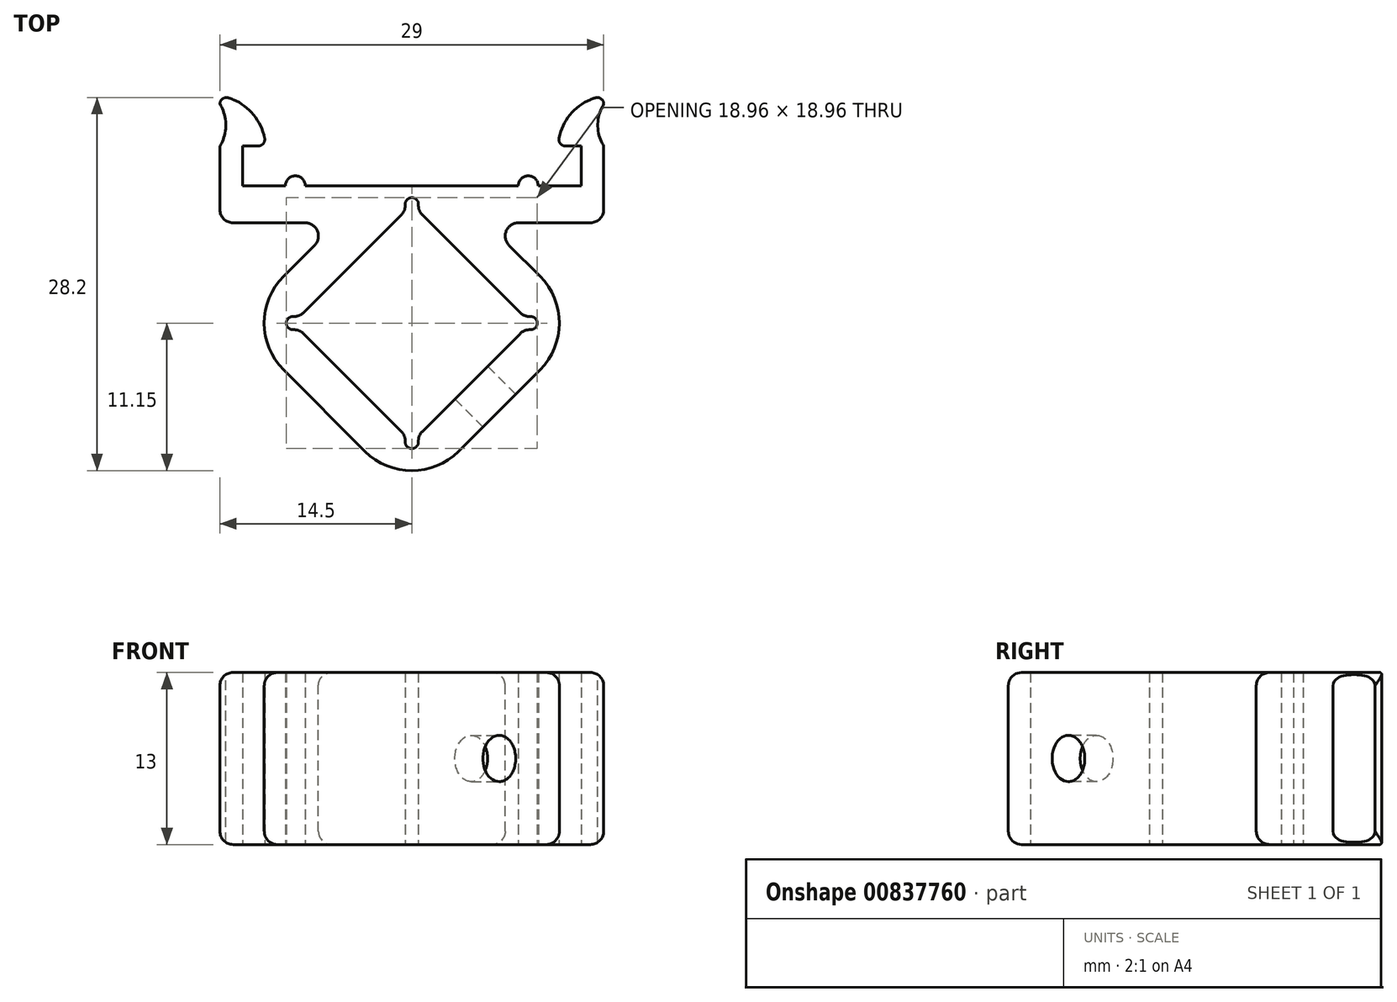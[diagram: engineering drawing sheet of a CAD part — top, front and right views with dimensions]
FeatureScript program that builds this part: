
annotation { "Feature Type Name" : "Feature", "Feature Type Description" : "" }
export const myFeature = defineFeature(function(context is Context, id is Id, definition is map)
    precondition{}
    {
        {
            var Q0;
            Q0=qCreatedBy(makeId("Top.planeOp"),FACE);
            var sketch = newSketch(context, id + "F0", { "sketchPlane" : qUnion([Q0])});
            skLineSegment(sketch, "E0.bottom", {"start": v(-13.5, 0) * mm, "end": v(-5.64, 0) * mm});
            skLineSegment(sketch, "E0.left", {"start": v(-14.5, 1) * mm, "end": v(-14.5, 9.59) * mm});
            skLineSegment(sketch, "E0.right", {"start": v(14.5, 1) * mm, "end": v(14.5, 9.59) * mm});
            skPoint(sketch, "E1.visualSharp", {"position": v(-14.5, 0) * mm});
            skArc(sketch, "E1.filletArc", {"start": v(-14.5, 1) * mm, "mid": v(-14.2, 0.3) * mm, "end": v(-13.5, 0) * mm});
            skPoint(sketch, "E2.visualSharp", {"position": v(14.5, 0) * mm});
            skArc(sketch, "E2.filletArc", {"start": v(13.5, 0) * mm, "mid": v(14.2, 0.3) * mm, "end": v(14.5, 1) * mm});
            skLineSegment(sketch, "E3", {"start": v(-12.8, 2.8) * mm, "end": v(-9.55, 2.8) * mm});
            skPoint(sketch, "E4", {"position": v(0, 2.8) * mm});
            skPoint(sketch, "E4.positionSnap0", {"position": v(0, 2.8) * mm});
            skLineSegment(sketch, "E5", {"start": v(-12.8, 2.8) * mm, "end": v(-12.8, 5.8) * mm});
            skLineSegment(sketch, "E6", {"start": v(-12.8, 5.8) * mm, "end": v(-11.05, 5.8) * mm});
            skLineSegment(sketch, "E7", {"start": v(12.8, 2.8) * mm, "end": v(12.8, 5.8) * mm});
            skLineSegment(sketch, "E8", {"start": v(12.8, 5.8) * mm, "end": v(11.05, 5.8) * mm});
            skArc(sketch, "E9", {"start": v(-11.05, 5.8) * mm, "mid": v(-12.09, 8.32) * mm, "end": v(-14.5, 9.59) * mm});
            skArc(sketch, "E10", {"start": v(14.5, 9.59) * mm, "mid": v(12.09, 8.32) * mm, "end": v(11.05, 5.8) * mm});
            skPoint(sketch, "E11", {"position": v(-8.8, 2.8) * mm});
            skPoint(sketch, "E12", {"position": v(8.8, 2.8) * mm});
            skArc(sketch, "E13", {"start": v(-8.05, 2.8) * mm, "mid": v(-8.8, 3.55) * mm, "end": v(-9.55, 2.8) * mm});
            skArc(sketch, "E14", {"start": v(9.55, 2.8) * mm, "mid": v(8.8, 3.55) * mm, "end": v(8.05, 2.8) * mm});
            skLineSegment(sketch, "E15.trimOffspring", {"start": v(-8.05, 2.8) * mm, "end": v(8.05, 2.8) * mm});
            skLineSegment(sketch, "E16.trimOffspring", {"start": v(9.55, 2.8) * mm, "end": v(12.8, 2.8) * mm});
            skLineSegment(sketch, "E17", {"start": v(0, 2.8) * mm, "end": v(0, 1.4) * mm, "construction": true});
            skLineSegment(sketch, "E18", {"start": v(-0.35, 1.05) * mm, "end": v(-8.63, -7.23) * mm});
            skLineSegment(sketch, "E19", {"start": v(-8.63, -7.93) * mm, "end": v(-0.35, -16.2) * mm});
            skLineSegment(sketch, "E20", {"start": v(0.35, -16.2) * mm, "end": v(8.63, -7.93) * mm});
            skLineSegment(sketch, "E21", {"start": v(8.63, -7.23) * mm, "end": v(0.35, 1.05) * mm});
            skLineSegment(sketch, "E22.0", {"start": v(-5.64, 0) * mm, "end": v(-13.22, -7.58) * mm});
            skLineSegment(sketch, "E22.1", {"start": v(13.22, -7.58) * mm, "end": v(5.64, 0) * mm});
            skLineSegment(sketch, "E22.2", {"start": v(0, -20.8) * mm, "end": v(13.22, -7.58) * mm});
            skLineSegment(sketch, "E22.3", {"start": v(-13.22, -7.58) * mm, "end": v(0, -20.8) * mm});
            skLineSegment(sketch, "E23.trimOffspring", {"start": v(5.64, 0) * mm, "end": v(13.5, 0) * mm});
            skArc(sketch, "E24", {"start": v(0.35, 1.05) * mm, "mid": v(0, 1.9) * mm, "end": v(-0.35, 1.05) * mm});
            skArc(sketch, "E25", {"start": v(8.63, -7.93) * mm, "mid": v(9.48, -7.58) * mm, "end": v(8.63, -7.23) * mm});
            skArc(sketch, "E26", {"start": v(-0.35, -16.2) * mm, "mid": v(0, -17.06) * mm, "end": v(0.35, -16.2) * mm});
            skArc(sketch, "E27", {"start": v(-8.63, -7.23) * mm, "mid": v(-9.48, -7.58) * mm, "end": v(-8.63, -7.93) * mm});
            skLineSegment(sketch, "E28.trimOffspring", {"start": v(0, 0.9) * mm, "end": v(0, 0) * mm, "construction": true});
            skSolve(sketch);
        }
        {
            var Q0;
            Q0 = qSketchRegion(id + "F0", true);
            extrude(context, id + "F1", {"entities" : qUnion([Q0]), "depth" : 13 * mm, "offsetDistance" : 25 * mm});
        }
        {
            var Q0;
            Q0=makeQuery(id+"F1.opExtrude","SWEPT_FACE",FACE,{"disambiguationData":[OSD([sQuery(id+"F0.wireOp",EDGE,"E15.trimOffspring")])]});
            var sketch = newSketch(context, id + "F2", { "sketchPlane" : qUnion([Q0])});
            skLineSegment(sketch, "E29", {"start": v(0, 0) * mm, "end": v(0, 13) * mm, "construction": true});
            skCircle(sketch, "E30", {"center": v(0, 6.5) * mm, "radius": 2 * mm});
            skSolve(sketch);
        }
        {
            var Q0;
            Q0=makeQuery(id+"F1.opExtrude","CAP_FACE",FACE,{"disambiguationData":[OSD([sQuery(id+"F0.wireOp",EDGE,"E0.bottom"),sQuery(id+"F0.wireOp",EDGE,"E0.left"),sQuery(id+"F0.wireOp",EDGE,"E0.right"),sQuery(id+"F0.wireOp",EDGE,"E1.filletArc"),sQuery(id+"F0.wireOp",EDGE,"E2.filletArc"),sQuery(id+"F0.wireOp",EDGE,"E3"),sQuery(id+"F0.wireOp",EDGE,"E5"),sQuery(id+"F0.wireOp",EDGE,"E6"),sQuery(id+"F0.wireOp",EDGE,"E7"),sQuery(id+"F0.wireOp",EDGE,"E8"),sQuery(id+"F0.wireOp",EDGE,"E9"),sQuery(id+"F0.wireOp",EDGE,"E10"),sQuery(id+"F0.wireOp",EDGE,"E13"),sQuery(id+"F0.wireOp",EDGE,"E14"),sQuery(id+"F0.wireOp",EDGE,"E15.trimOffspring"),sQuery(id+"F0.wireOp",EDGE,"E16.trimOffspring")])],"isStart":false});
            var sketch = newSketch(context, id + "F3", { "sketchPlane" : qUnion([Q0])});
            skLineSegment(sketch, "E31.0.0", {"start": v(8.05, 2.8) * mm, "end": v(-8.05, 2.8) * mm});
            skArc(sketch, "E31.0.1", {"start": v(-8.05, 2.8) * mm, "mid": v(-8.8, 3.55) * mm, "end": v(-9.55, 2.8) * mm});
            skLineSegment(sketch, "E31.0.2", {"start": v(-9.55, 2.8) * mm, "end": v(-12.8, 2.8) * mm});
            skLineSegment(sketch, "E31.0.3", {"start": v(-12.8, 2.8) * mm, "end": v(-12.8, 5.8) * mm});
            skLineSegment(sketch, "E31.0.4", {"start": v(-12.8, 5.8) * mm, "end": v(-11.05, 5.8) * mm});
            skArc(sketch, "E31.0.5", {"start": v(-11.05, 5.8) * mm, "mid": v(-11.88, 8.06) * mm, "end": v(-13.85, 9.44) * mm});
            skLineSegment(sketch, "E31.0.6", {"start": v(-14.5, 8.97) * mm, "end": v(-14.5, 5.8) * mm});
            skArc(sketch, "E31.0.7", {"start": v(-14.5, 1) * mm, "mid": v(-14.2, 0.3) * mm, "end": v(-13.5, 0) * mm});
            skLineSegment(sketch, "E31.0.8", {"start": v(-13.5, 0) * mm, "end": v(-13.5, 0) * mm});
            skArc(sketch, "E31.0.9", {"start": v(13.5, 0) * mm, "mid": v(14.2, 0.3) * mm, "end": v(14.5, 1) * mm});
            skLineSegment(sketch, "E31.0.10", {"start": v(14.5, 1) * mm, "end": v(14.5, 5.8) * mm});
            skArc(sketch, "E31.0.11", {"start": v(13.85, 9.44) * mm, "mid": v(11.88, 8.06) * mm, "end": v(11.05, 5.8) * mm});
            skLineSegment(sketch, "E31.0.12", {"start": v(11.05, 5.8) * mm, "end": v(12.8, 5.8) * mm});
            skLineSegment(sketch, "E31.0.13", {"start": v(12.8, 5.8) * mm, "end": v(12.8, 2.8) * mm});
            skLineSegment(sketch, "E31.0.14", {"start": v(12.8, 2.8) * mm, "end": v(9.55, 2.8) * mm});
            skArc(sketch, "E31.0.15", {"start": v(9.55, 2.8) * mm, "mid": v(8.8, 3.55) * mm, "end": v(8.05, 2.8) * mm});
            skLineSegment(sketch, "E32", {"start": v(-12.8, 5.8) * mm, "end": v(-15.05, 5.8) * mm, "construction": true});
            skLineSegment(sketch, "E33", {"start": v(-14.5, 5.8) * mm, "end": v(-14.5, 1) * mm});
            skPoint(sketch, "E34.visualSharp", {"position": v(-14.5, 9.59) * mm});
            skArc(sketch, "E34.filletArc", {"start": v(-13.85, 9.44) * mm, "mid": v(-14.3, 9.37) * mm, "end": v(-14.5, 8.97) * mm});
            skPoint(sketch, "E35.visualSharp", {"position": v(14.5, 9.59) * mm});
            skArc(sketch, "E35.filletArc", {"start": v(14.5, 8.97) * mm, "mid": v(14.3, 9.37) * mm, "end": v(13.85, 9.44) * mm});
            skArc(sketch, "E36", {"start": v(-14.5, 5.8) * mm, "mid": v(-14.05, 7.38) * mm, "end": v(-14.5, 8.97) * mm});
            skLineSegment(sketch, "E37", {"start": v(-14.5, 8.97) * mm, "end": v(-14.5, 9.59) * mm});
            skLineSegment(sketch, "E38", {"start": v(-14.5, 9.59) * mm, "end": v(-13.85, 9.44) * mm});
            skLineSegment(sketch, "E39", {"start": v(12.8, 5.8) * mm, "end": v(14.5, 5.8) * mm, "construction": true});
            skLineSegment(sketch, "E40", {"start": v(14.5, 5.8) * mm, "end": v(14.5, 8.97) * mm});
            skArc(sketch, "E41", {"start": v(14.5, 8.97) * mm, "mid": v(14.05, 7.38) * mm, "end": v(14.5, 5.8) * mm});
            skLineSegment(sketch, "E42", {"start": v(13.85, 9.44) * mm, "end": v(14.5, 9.59) * mm});
            skLineSegment(sketch, "E43", {"start": v(14.5, 9.59) * mm, "end": v(14.5, 8.97) * mm});
            skSolve(sketch);
        }
        {
            var Q0;
            Q0=makeQuery(id+"F3.imprint","IMPRINT",FACE,{"disambiguationData":[TD([[makeQuery(id+"F3.imprint","IMPRINT",EDGE,{"derivedFrom":sQuery(id+"F3.wireOp",EDGE,"E31.0.6")}),-1.0]])]});
            var Q1;
            Q1=makeQuery(id+"F3.imprint","IMPRINT",FACE,{"disambiguationData":[TD([[makeQuery(id+"F3.imprint","IMPRINT",EDGE,{"derivedFrom":sQuery(id+"F3.wireOp",EDGE,"E40")}),1.0]])]});
            extrude(context, id + "F4", {"entities" : qUnion([Q0, Q1]), "operationType" : NewBodyOperationType.REMOVE, "endBound" : BoundingType.THROUGH_ALL, "oppositeDirection" : true, "depth" : 25 * mm, "offsetDistance" : 25 * mm});
        }
        {
            var Q0;
            Q0=makeQuery(id+"F1.opExtrude","SWEPT_EDGE",EDGE,{"disambiguationData":[OSD([sQuery(id+"F0.wireOp",EDGE,"E0.left"),sQuery(id+"F0.wireOp",EDGE,"E9")])]});
            var Q1;
            Q1=makeQuery(id+"F1.opExtrude","SWEPT_EDGE",EDGE,{"disambiguationData":[OSD([sQuery(id+"F0.wireOp",EDGE,"E0.right"),sQuery(id+"F0.wireOp",EDGE,"E10")])]});
            fillet(context, id + "F5", {"entities" : qUnion([Q0, Q1]), "radius" : .5 * mm, "tangentPropagation" : true, "allowEdgeOverflow" : false});
        }
        {
            var Q0;
            Q0=makeQuery(id+"F1.opExtrude","SWEPT_EDGE",EDGE,{"disambiguationData":[OSD([sQuery(id+"F0.wireOp",EDGE,"E0.bottom"),sQuery(id+"F0.wireOp",EDGE,"E22.0")])]});
            var Q1;
            Q1=makeQuery(id+"F1.opExtrude","SWEPT_EDGE",EDGE,{"disambiguationData":[OSD([sQuery(id+"F0.wireOp",EDGE,"E22.1"),sQuery(id+"F0.wireOp",EDGE,"E23.trimOffspring")])]});
            fillet(context, id + "F6", {"entities" : qUnion([Q0, Q1]), "radius" : 1 * mm, "tangentPropagation" : true, "allowEdgeOverflow" : false});
        }
        {
            var Q0;
            Q0=makeQuery(id+"F1.opExtrude","SWEPT_EDGE",EDGE,{"disambiguationData":[OSD([sQuery(id+"F0.wireOp",EDGE,"E22.0"),sQuery(id+"F0.wireOp",EDGE,"E22.3")])]});
            var Q1;
            Q1=makeQuery(id+"F1.opExtrude","SWEPT_EDGE",EDGE,{"disambiguationData":[OSD([sQuery(id+"F0.wireOp",EDGE,"E22.2"),sQuery(id+"F0.wireOp",EDGE,"E22.3")])]});
            var Q2;
            Q2=makeQuery(id+"F1.opExtrude","SWEPT_EDGE",EDGE,{"disambiguationData":[OSD([sQuery(id+"F0.wireOp",EDGE,"E22.1"),sQuery(id+"F0.wireOp",EDGE,"E22.2")])]});
            fillet(context, id + "F7", {"entities" : qUnion([Q0, Q1, Q2]), "radius" : 5 * mm, "tangentPropagation" : true, "allowEdgeOverflow" : false});
        }
        {
            var Q0;
            Q0=makeQuery(id+"F1.opExtrude","CAP_EDGE",EDGE,{"disambiguationData":[OSD([sQuery(id+"F0.wireOp",EDGE,"E22.3")])],"isStart":false});
            var Q1;
            Q1=makeQuery(id+"F1.opExtrude","CAP_EDGE",EDGE,{"disambiguationData":[OSD([sQuery(id+"F0.wireOp",EDGE,"E22.3")])],"isStart":true});
            fillet(context, id + "F8", {"entities" : qUnion([Q0, Q1]), "radius" : 1 * mm, "tangentPropagation" : true, "allowEdgeOverflow" : false});
        }
        {
            var Q0;
            Q0=makeQuery(id+"F1.opExtrude","SWEPT_EDGE",EDGE,{"disambiguationData":[OSD([sQuery(id+"F0.wireOp",EDGE,"E6"),sQuery(id+"F0.wireOp",EDGE,"E9")])]});
            var Q1;
            Q1=makeQuery(id+"F1.opExtrude","SWEPT_EDGE",EDGE,{"disambiguationData":[OSD([sQuery(id+"F0.wireOp",EDGE,"E8"),sQuery(id+"F0.wireOp",EDGE,"E10")])]});
            fillet(context, id + "F9", {"entities" : qUnion([Q0, Q1]), "radius" : .5 * mm, "tangentPropagation" : true, "allowEdgeOverflow" : false});
        }
        {
            var Q0;
            Q0=makeQuery(id+"F1.opExtrude","SWEPT_EDGE",EDGE,{"disambiguationData":[OSD([sQuery(id+"F0.wireOp",EDGE,"E18"),sQuery(id+"F0.wireOp",EDGE,"E24")])]});
            var Q1;
            Q1=makeQuery(id+"F1.opExtrude","SWEPT_EDGE",EDGE,{"disambiguationData":[OSD([sQuery(id+"F0.wireOp",EDGE,"E21"),sQuery(id+"F0.wireOp",EDGE,"E24")])]});
            var Q2;
            Q2=makeQuery(id+"F1.opExtrude","SWEPT_EDGE",EDGE,{"disambiguationData":[OSD([sQuery(id+"F0.wireOp",EDGE,"E18"),sQuery(id+"F0.wireOp",EDGE,"E27")])]});
            var Q3;
            Q3=makeQuery(id+"F1.opExtrude","SWEPT_EDGE",EDGE,{"disambiguationData":[OSD([sQuery(id+"F0.wireOp",EDGE,"E19"),sQuery(id+"F0.wireOp",EDGE,"E27")])]});
            var Q4;
            Q4=makeQuery(id+"F1.opExtrude","SWEPT_EDGE",EDGE,{"disambiguationData":[OSD([sQuery(id+"F0.wireOp",EDGE,"E19"),sQuery(id+"F0.wireOp",EDGE,"E26")])]});
            var Q5;
            Q5=makeQuery(id+"F1.opExtrude","SWEPT_EDGE",EDGE,{"disambiguationData":[OSD([sQuery(id+"F0.wireOp",EDGE,"E20"),sQuery(id+"F0.wireOp",EDGE,"E26")])]});
            var Q6;
            Q6=makeQuery(id+"F1.opExtrude","SWEPT_EDGE",EDGE,{"disambiguationData":[OSD([sQuery(id+"F0.wireOp",EDGE,"E21"),sQuery(id+"F0.wireOp",EDGE,"E25")])]});
            var Q7;
            Q7=makeQuery(id+"F1.opExtrude","SWEPT_EDGE",EDGE,{"disambiguationData":[OSD([sQuery(id+"F0.wireOp",EDGE,"E20"),sQuery(id+"F0.wireOp",EDGE,"E25")])]});
            fillet(context, id + "F10", {"entities" : qUnion([Q0, Q1, Q2, Q3, Q4, Q5, Q6, Q7]), "radius" : 1 * mm, "tangentPropagation" : true, "allowEdgeOverflow" : false});
        }
        {
            var Q0;
            Q0=makeQuery(id+"F1.opExtrude","SWEPT_FACE",FACE,{"disambiguationData":[OSD([sQuery(id+"F0.wireOp",EDGE,"E22.2")])]});
            var sketch = newSketch(context, id + "F11", { "sketchPlane" : qUnion([Q0])});
            skLineSegment(sketch, "E44", {"start": v(-1.01, 6.5) * mm, "end": v(-9.71, 6.5) * mm, "construction": true});
            skCircle(sketch, "E45", {"center": v(-5.36, 6.5) * mm, "radius": 1.75 * mm});
            skSolve(sketch);
        }
        {
            var Q0;
            Q0=makeQuery(id+"F11.imprint","IMPRINT",FACE,{"disambiguationData":[TD([[makeQuery(id+"F11.imprint","IMPRINT",EDGE,{"derivedFrom":sQuery(id+"F11.wireOp",EDGE,"E45")}),1.0]])]});
            var Q1;
            Q1=makeQuery(id+"F1.opExtrude","SWEPT_FACE",FACE,{"disambiguationData":[OSD([sQuery(id+"F0.wireOp",EDGE,"E18")])]});
            extrude(context, id + "F12", {"entities" : qUnion([Q0]), "operationType" : NewBodyOperationType.REMOVE, "endBound" : BoundingType.UP_TO_SURFACE, "oppositeDirection" : true, "depth" : 25 * mm, "endBoundEntityFace" : qUnion([Q1]), "offsetDistance" : 25 * mm});
        }
    });
